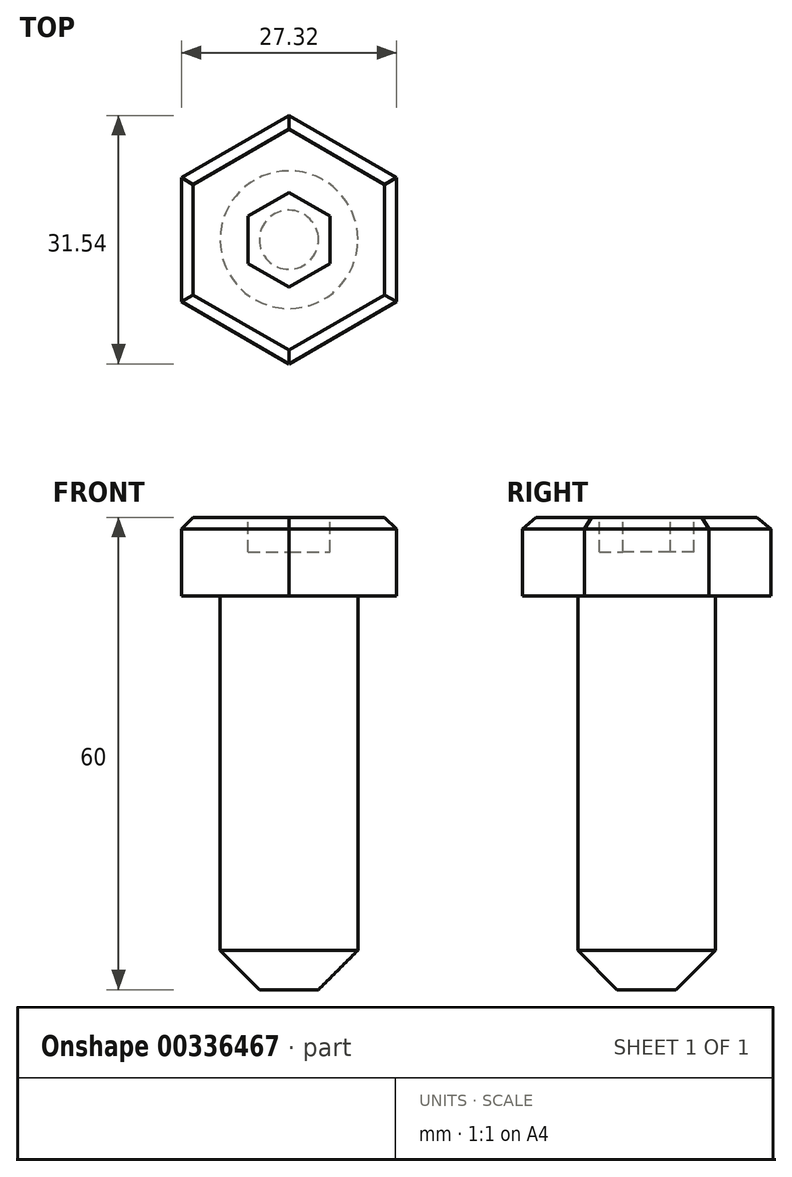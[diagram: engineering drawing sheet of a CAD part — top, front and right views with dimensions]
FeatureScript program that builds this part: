
annotation { "Feature Type Name" : "Feature", "Feature Type Description" : "" }
export const myFeature = defineFeature(function(context is Context, id is Id, definition is map)
    precondition{}
    {
        {
            var Q0;
            Q0=qCreatedBy(makeId("Top.planeOp"),FACE);
            var sketch = newSketch(context, id + "F0", { "sketchPlane" : qUnion([Q0])});
            skCircle(sketch, "E0", {"center": v(0, 0) * mm, "radius": 8.75 * mm});
            skCircle(sketch, "E1.cCircle", {"center": v(0, 0) * mm, "radius": 13.66 * mm, "construction": true});
            skLineSegment(sketch, "E1.0", {"start": v(13.66, 7.88) * mm, "end": v(13.66, -7.88) * mm});
            skLineSegment(sketch, "E1.1", {"start": v(13.66, -7.88) * mm, "end": v(0, -15.77) * mm});
            skLineSegment(sketch, "E1.2", {"start": v(0, -15.77) * mm, "end": v(-13.66, -7.88) * mm});
            skLineSegment(sketch, "E1.3", {"start": v(-13.66, -7.88) * mm, "end": v(-13.66, 7.88) * mm});
            skLineSegment(sketch, "E1.4", {"start": v(-13.66, 7.88) * mm, "end": v(0, 15.77) * mm});
            skLineSegment(sketch, "E1.5", {"start": v(0, 15.77) * mm, "end": v(13.66, 7.88) * mm});
            skPoint(sketch, "E1.0.midPoint", {"position": v(13.66, 0) * mm});
            skSolve(sketch);
        }
        {
            var Q0;
            Q0=makeQuery(id+"F0.imprint","IMPRINT",FACE,{"disambiguationData":[TD([[makeQuery(id+"F0.imprint","IMPRINT",EDGE,{"derivedFrom":sQuery(id+"F0.wireOp",EDGE,"E0")}),1.0]])]});
            extrude(context, id + "F1", {"entities" : qUnion([Q0]), "oppositeDirection" : true, "depth" : 60 * mm});
        }
        {
            var Q0;
            Q0=makeQuery(id+"F0.imprint","IMPRINT",FACE,{"disambiguationData":[TD([[makeQuery(id+"F0.imprint","IMPRINT",EDGE,{"derivedFrom":sQuery(id+"F0.wireOp",EDGE,"E0")}),-1.0]])]});
            var Q1;
            Q1=makeQuery(id+"F0.imprint","IMPRINT",FACE,{"disambiguationData":[TD([[makeQuery(id+"F0.imprint","IMPRINT",EDGE,{"derivedFrom":sQuery(id+"F0.wireOp",EDGE,"E0")}),1.0]])]});
            extrude(context, id + "F2", {"entities" : qUnion([Q0, Q1]), "operationType" : NewBodyOperationType.ADD, "oppositeDirection" : true, "depth" : 10 * mm});
        }
        {
            var Q0;
            Q0=makeQuery(id+"F1.opExtrude","CAP_EDGE",EDGE,{"disambiguationData":[OSD([sQuery(id+"F0.wireOp",EDGE,"E0")])],"isStart":false});
            chamfer(context, id + "F3", {"entities" : qUnion([Q0]), "width" : 5 * mm, "tangentPropagation" : true});
        }
        {
            var Q0;
            Q0=makeQuery(id+"F2.boolean.opBoolean","MERGE",FACE,{"derivedFrom":[makeQuery(id+"F1.opExtrude","CAP_FACE",FACE,{"disambiguationData":[OSD([sQuery(id+"F0.wireOp",EDGE,"E0")])],"isStart":true}),makeQuery(id+"F2.opExtrude","CAP_FACE",FACE,{"disambiguationData":[OSD([sQuery(id+"F0.wireOp",EDGE,"E1.0"),sQuery(id+"F0.wireOp",EDGE,"E1.1"),sQuery(id+"F0.wireOp",EDGE,"E1.2"),sQuery(id+"F0.wireOp",EDGE,"E1.3"),sQuery(id+"F0.wireOp",EDGE,"E1.4"),sQuery(id+"F0.wireOp",EDGE,"E1.5")])],"isStart":true})]});
            var sketch = newSketch(context, id + "F4", { "sketchPlane" : qUnion([Q0])});
            skCircle(sketch, "E2.cCircle", {"center": v(0, 0) * mm, "radius": 5.2 * mm, "construction": true});
            skLineSegment(sketch, "E2.0", {"start": v(5.2, 3) * mm, "end": v(5.2, -3) * mm});
            skLineSegment(sketch, "E2.1", {"start": v(5.2, -3) * mm, "end": v(0, -6) * mm});
            skLineSegment(sketch, "E2.2", {"start": v(0, -6) * mm, "end": v(-5.2, -3) * mm});
            skLineSegment(sketch, "E2.3", {"start": v(-5.2, -3) * mm, "end": v(-5.2, 3) * mm});
            skLineSegment(sketch, "E2.4", {"start": v(-5.2, 3) * mm, "end": v(0, 6) * mm});
            skLineSegment(sketch, "E2.5", {"start": v(0, 6) * mm, "end": v(5.2, 3) * mm});
            skPoint(sketch, "E2.0.midPoint", {"position": v(5.2, 0) * mm});
            skSolve(sketch);
        }
        {
            var Q0;
            Q0=makeQuery(id+"F4.imprint","IMPRINT",FACE,{"disambiguationData":[TD([[makeQuery(id+"F4.imprint","IMPRINT",EDGE,{"derivedFrom":sQuery(id+"F4.wireOp",EDGE,"E2.0")}),-1.0]])]});
            extrude(context, id + "F5", {"entities" : qUnion([Q0]), "operationType" : NewBodyOperationType.REMOVE, "oppositeDirection" : true, "depth" : 4.4 * mm});
        }
        {
            var Q0;
            Q0=makeQuery(id+"F2.opExtrude","CAP_EDGE",EDGE,{"disambiguationData":[OSD([sQuery(id+"F0.wireOp",EDGE,"E1.2")])],"isStart":true});
            var Q1;
            Q1=makeQuery(id+"F2.opExtrude","CAP_EDGE",EDGE,{"disambiguationData":[OSD([sQuery(id+"F0.wireOp",EDGE,"E1.1")])],"isStart":true});
            var Q2;
            Q2=makeQuery(id+"F2.opExtrude","CAP_EDGE",EDGE,{"disambiguationData":[OSD([sQuery(id+"F0.wireOp",EDGE,"E1.0")])],"isStart":true});
            var Q3;
            Q3=makeQuery(id+"F2.opExtrude","CAP_EDGE",EDGE,{"disambiguationData":[OSD([sQuery(id+"F0.wireOp",EDGE,"E1.5")])],"isStart":true});
            var Q4;
            Q4=makeQuery(id+"F2.opExtrude","CAP_EDGE",EDGE,{"disambiguationData":[OSD([sQuery(id+"F0.wireOp",EDGE,"E1.4")])],"isStart":true});
            var Q5;
            Q5=makeQuery(id+"F2.opExtrude","CAP_EDGE",EDGE,{"disambiguationData":[OSD([sQuery(id+"F0.wireOp",EDGE,"E1.3")])],"isStart":true});
            chamfer(context, id + "F6", {"entities" : qUnion([Q0, Q1, Q2, Q3, Q4, Q5]), "width" : 1.5 * mm, "tangentPropagation" : true});
        }
    });
